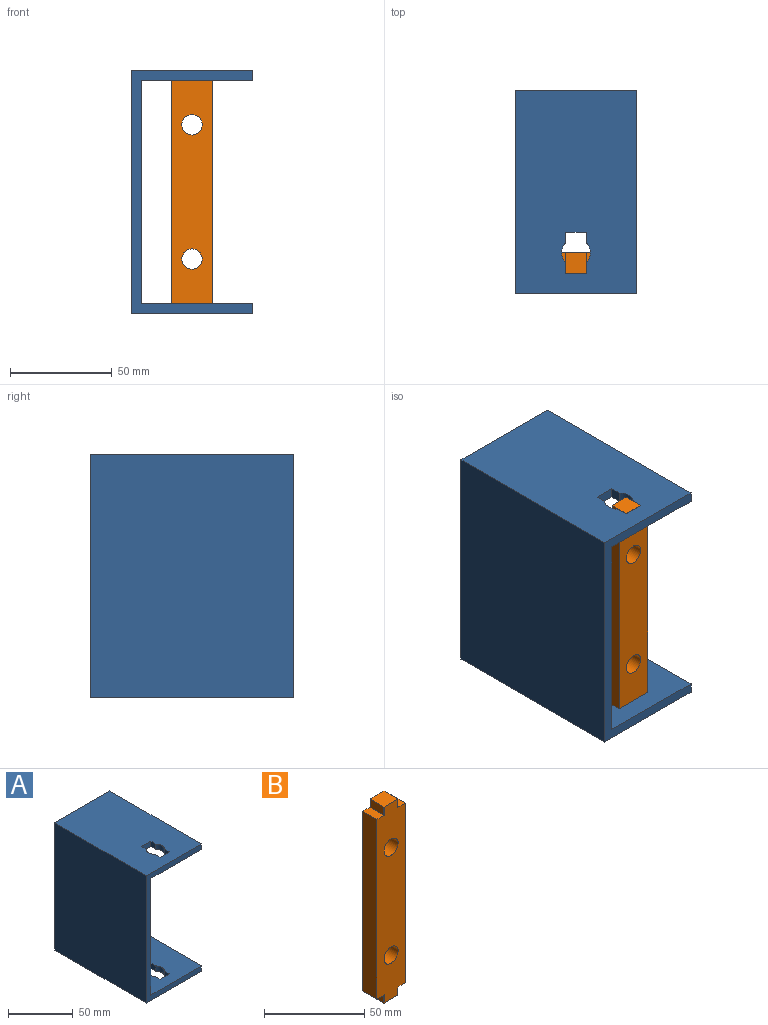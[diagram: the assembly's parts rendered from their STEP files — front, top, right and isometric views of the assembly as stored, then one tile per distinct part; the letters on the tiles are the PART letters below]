
ASSEMBLY  parts=2 mates=1
PART A: 26 faces, bbox 60x100x120 mm
  f0: plane 100x55mm, normal (0,0,-1), area 5270mm2, adj f4,f5,f8,f9,f18,f19,f20,f21
  f1: plane 100x60mm, normal (0,0,1), area 5770mm2, adj f5,f6,f8,f9,f18,f19,f20,f21
  f2: plane 100x60mm, normal (0,0,-1), area 5770mm2, adj f6,f7,f8,f9,f10,f11,f12,f13
  f3: plane 100x55mm, normal (0,0,1), area 5270mm2, adj f4,f7,f8,f9,f10,f11,f12,f13
  f4: plane 110x100mm, normal (1,0,0), area 11000mm2, adj f0,f3,f8,f9
  f5: plane 100x5mm, normal (1,0,0), area 500mm2, adj f0,f1,f8,f9
  f6: plane 120x100mm, normal (-1,0,0), area 12000mm2, adj f1,f2,f8,f9
  f7: plane 100x5mm, normal (1,0,0), area 500mm2, adj f2,f3,f8,f9
  f8: plane 120x60mm, normal (0,-1,0), area 1150mm2, adj f0,f1,f2,f3,f4,f5,f6,f7
  f9: plane 120x60mm, normal (0,1,0), area 1150mm2, adj f0,f1,f2,f3,f4,f5,f6,f7
  f10: plane 5.25x5mm, normal (-1,0,0), area 26.3mm2, adj f2,f3,f11,f17
  f11: cylinder r=7mm len=9.7mm, axis (0,0,1), area 53.5mm2, adj f2,f3,f10,f12
  f12: plane 5.25x5mm, normal (-1,0,0), area 26.3mm2, adj f2,f3,f11,f13
  f13: plane 10.1x5mm, normal (0,1,0), area 50.5mm2, adj f2,f3,f12,f14
  f14: plane 5.25x5mm, normal (1,0,0), area 26.3mm2, adj f2,f3,f13,f15
  f15: cylinder r=7mm len=9.7mm, axis (0,0,1), area 53.5mm2, adj f2,f3,f14,f16
  f16: plane 5.25x5mm, normal (1,0,0), area 26.3mm2, adj f2,f3,f15,f17
  f17: plane 10.1x5mm, normal (0,-1,0), area 50.5mm2, adj f2,f3,f10,f16
  f18: plane 10.1x5mm, normal (0,-1,0), area 50.5mm2, adj f0,f1,f19,f25
  f19: plane 5.25x5mm, normal (1,0,0), area 26.3mm2, adj f0,f1,f18,f20
  f20: cylinder r=7mm len=9.7mm, axis (0,0,1), area 53.5mm2, adj f0,f1,f19,f21
  f21: plane 5.25x5mm, normal (1,0,0), area 26.3mm2, adj f0,f1,f20,f22
  f22: plane 10.1x5mm, normal (0,1,0), area 50.5mm2, adj f0,f1,f21,f23
  f23: plane 5.25x5mm, normal (-1,0,0), area 26.3mm2, adj f0,f1,f22,f24
  f24: cylinder r=7mm len=9.7mm, axis (0,0,1), area 53.5mm2, adj f0,f1,f23,f25
  f25: plane 5.25x5mm, normal (-1,0,0), area 26.3mm2, adj f0,f1,f18,f24
PART B: 24 faces, bbox 20x10x120 mm
  f0: plane 9.6x5mm, normal (-1,0,0), area 48mm2, adj f1,f12,f17,f19
  f1: plane 10x10mm, normal (0,0,-1), area 99.9mm2, adj f0,f2,f14,f15,f17,f18,f19,f20
  f2: plane 9.6x5mm, normal (1,0,0), area 48mm2, adj f1,f3,f18,f20
  f3: plane 10x5.2mm, normal (0,0,-1), area 50mm2, adj f2,f4,f14,f15,f18,f20
  f4: plane 110x10mm, normal (1,0,0), area 1100mm2, adj f3,f5,f14,f15
  f5: plane 10x5.2mm, normal (0,0,1), area 50mm2, adj f4,f6,f14,f15,f21,f23
  f6: plane 9.6x5mm, normal (1,0,0), area 48mm2, adj f5,f7,f21,f23
  f7: plane 10x10mm, normal (0,0,1), area 99.9mm2, adj f6,f8,f14,f15,f16,f21,f22,f23
  f8: plane 9.6x5mm, normal (-1,0,0), area 48mm2, adj f7,f9,f16,f22
  f9: plane 10x5.2mm, normal (0,0,1), area 50mm2, adj f8,f10,f14,f15,f16,f22
  f10: plane 110x10mm, normal (-1,0,0), area 1100mm2, adj f9,f12,f14,f15
  f11: cylinder r=5mm len=10mm, axis (0,1,0), area 314.2mm2, adj f14,f15
  f12: plane 10x5.2mm, normal (0,0,-1), area 50mm2, adj f0,f10,f14,f15,f17,f19
  f13: cylinder r=5mm len=10mm, axis (0,1,0), area 314.2mm2, adj f14,f15
  f14: plane 120x20mm, normal (0,-1,0), area 2138.9mm2, adj f1,f3,f4,f5,f7,f9,f10,f11
  f15: plane 120x20mm, normal (0,1,0), area 2138.9mm2, adj f1,f3,f4,f5,f7,f9,f10,f11
  f16: plane 5x0.2mm, normal (-0.71,0.71,0), area 1.4mm2, adj f7,f8,f9,f15
  f17: plane 5x0.2mm, normal (-0.71,0.71,0), area 1.4mm2, adj f0,f1,f12,f15
  f18: plane 5x0.2mm, normal (0.71,0.71,0), area 1.4mm2, adj f1,f2,f3,f15
  f19: plane 5x0.2mm, normal (-0.71,-0.71,0), area 1.4mm2, adj f0,f1,f12,f14
  f20: plane 5x0.2mm, normal (0.71,-0.71,0), area 1.4mm2, adj f1,f2,f3,f14
  f21: plane 5x0.2mm, normal (0.71,0.71,0), area 1.4mm2, adj f5,f6,f7,f15
  f22: plane 5x0.2mm, normal (-0.71,-0.71,0), area 1.4mm2, adj f7,f8,f9,f14
  f23: plane 5x0.2mm, normal (0.71,-0.71,0), area 1.4mm2, adj f5,f6,f7,f14
PLACE A at identity fixed
PLACE B t=(0,-35,0)mm
MATE fastened A.f1 <-> B.f7  axis (0,0,1) through (0,-40,60)mm
